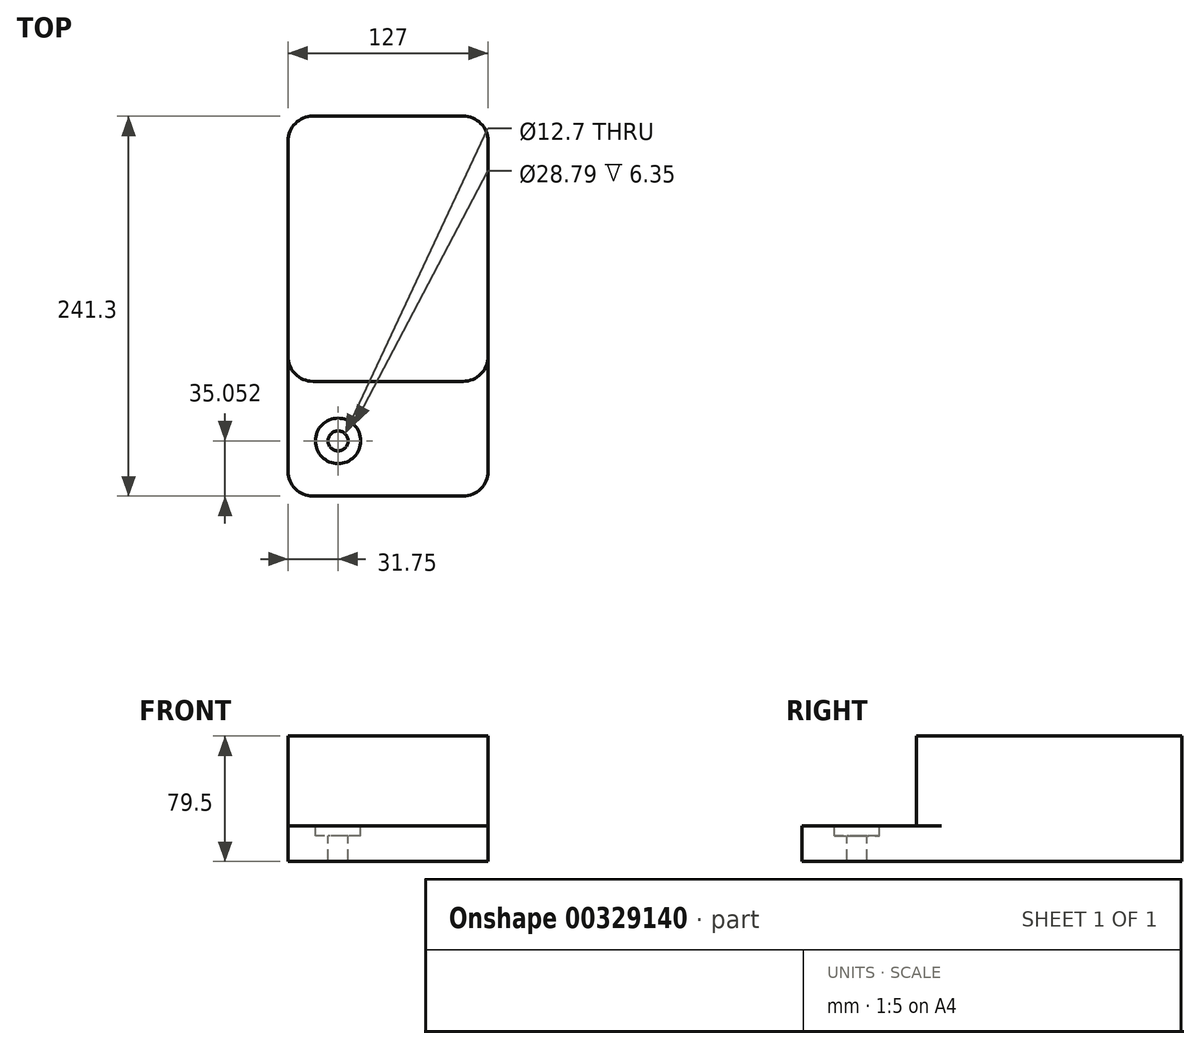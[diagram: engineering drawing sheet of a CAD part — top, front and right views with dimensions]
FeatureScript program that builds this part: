
annotation { "Feature Type Name" : "Feature", "Feature Type Description" : "" }
export const myFeature = defineFeature(function(context is Context, id is Id, definition is map)
    precondition{}
    {
        {
            var Q0;
            Q0=qCreatedBy(makeId("Right.planeOp"),FACE);
            var sketch = newSketch(context, id + "F0", { "sketchPlane" : qUnion([Q0])});
            skLineSegment(sketch, "E0", {"start": v(0, 0) * mm, "end": v(0, 22.35) * mm});
            skLineSegment(sketch, "E1", {"start": v(0, 22.35) * mm, "end": v(72.9, 22.35) * mm});
            skLineSegment(sketch, "E2", {"start": v(72.9, 22.35) * mm, "end": v(72.9, 79.5) * mm});
            skLineSegment(sketch, "E3", {"start": v(72.9, 79.5) * mm, "end": v(241.3, 79.5) * mm});
            skLineSegment(sketch, "E4", {"start": v(241.3, 79.5) * mm, "end": v(241.3, 0) * mm});
            skLineSegment(sketch, "E5", {"start": v(241.3, 0) * mm, "end": v(0, 0) * mm});
            skSolve(sketch);
        }
        {
            var Q0;
            Q0=makeQuery(id+"F0.imprint","IMPRINT",FACE,{"disambiguationData":[TD([[makeQuery(id+"F0.imprint","IMPRINT",EDGE,{"derivedFrom":sQuery(id+"F0.wireOp",EDGE,"E0")}),-1.0]])]});
            extrude(context, id + "F1", {"entities" : qUnion([Q0]), "depth" : 127 * mm});
        }
        {
            var Q0;
            Q0=makeQuery(id+"F1.opExtrude","SWEPT_FACE",FACE,{"disambiguationData":[OSD([sQuery(id+"F0.wireOp",EDGE,"E1")])]});
            var sketch = newSketch(context, id + "F2", { "sketchPlane" : qUnion([Q0])});
            skCircle(sketch, "E6", {"center": v(31.75, 35.05) * mm, "radius": 14.4 * mm});
            skSolve(sketch);
        }
        {
            var Q0;
            Q0=makeQuery(id+"F2.imprint","IMPRINT",FACE,{"disambiguationData":[TD([[makeQuery(id+"F2.imprint","IMPRINT",EDGE,{"derivedFrom":sQuery(id+"F2.wireOp",EDGE,"E6")}),1.0]])]});
            var sketch = newSketch(context, id + "F3", { "sketchPlane" : qUnion([Q0])});
            skCircle(sketch, "E7", {"center": v(31.75, 35.05) * mm, "radius": 6.35 * mm});
            skSolve(sketch);
        }
        {
            var Q0;
            Q0=makeQuery(id+"F3.imprint","IMPRINT",FACE,{"disambiguationData":[TD([[makeQuery(id+"F3.imprint","IMPRINT",EDGE,{"derivedFrom":sQuery(id+"F3.wireOp",EDGE,"E7")}),1.0]])]});
            extrude(context, id + "F4", {"entities" : qUnion([Q0]), "operationType" : NewBodyOperationType.REMOVE, "endBound" : BoundingType.THROUGH_ALL, "oppositeDirection" : true, "depth" : 25.4 * mm});
        }
        {
            var Q0;
            Q0=makeQuery(id+"F2.imprint","IMPRINT",FACE,{"disambiguationData":[TD([[makeQuery(id+"F2.imprint","IMPRINT",EDGE,{"derivedFrom":sQuery(id+"F2.wireOp",EDGE,"E6")}),1.0]])]});
            extrude(context, id + "F5", {"entities" : qUnion([Q0]), "operationType" : NewBodyOperationType.REMOVE, "oppositeDirection" : true, "depth" : 6.35 * mm});
        }
        {
            var Q0;
            Q0=makeQuery(id+"F1.opExtrude","CAP_EDGE",EDGE,{"disambiguationData":[OSD([sQuery(id+"F0.wireOp",EDGE,"E2")])],"isStart":false});
            var Q1;
            Q1=makeQuery(id+"F1.opExtrude","CAP_EDGE",EDGE,{"disambiguationData":[OSD([sQuery(id+"F0.wireOp",EDGE,"E0")])],"isStart":false});
            var Q2;
            Q2=makeQuery(id+"F1.opExtrude","CAP_EDGE",EDGE,{"disambiguationData":[OSD([sQuery(id+"F0.wireOp",EDGE,"E0")])],"isStart":true});
            var Q3;
            Q3=makeQuery(id+"F1.opExtrude","CAP_EDGE",EDGE,{"disambiguationData":[OSD([sQuery(id+"F0.wireOp",EDGE,"E2")])],"isStart":true});
            var Q4;
            Q4=makeQuery(id+"F1.opExtrude","CAP_EDGE",EDGE,{"disambiguationData":[OSD([sQuery(id+"F0.wireOp",EDGE,"E4")])],"isStart":true});
            var Q5;
            Q5=makeQuery(id+"F1.opExtrude","CAP_EDGE",EDGE,{"disambiguationData":[OSD([sQuery(id+"F0.wireOp",EDGE,"E4")])],"isStart":false});
            fillet(context, id + "F6", {"entities" : qUnion([Q0, Q1, Q2, Q3, Q4, Q5]), "radius" : 15.75 * mm, "tangentPropagation" : true, "allowEdgeOverflow" : false});
        }
    });
